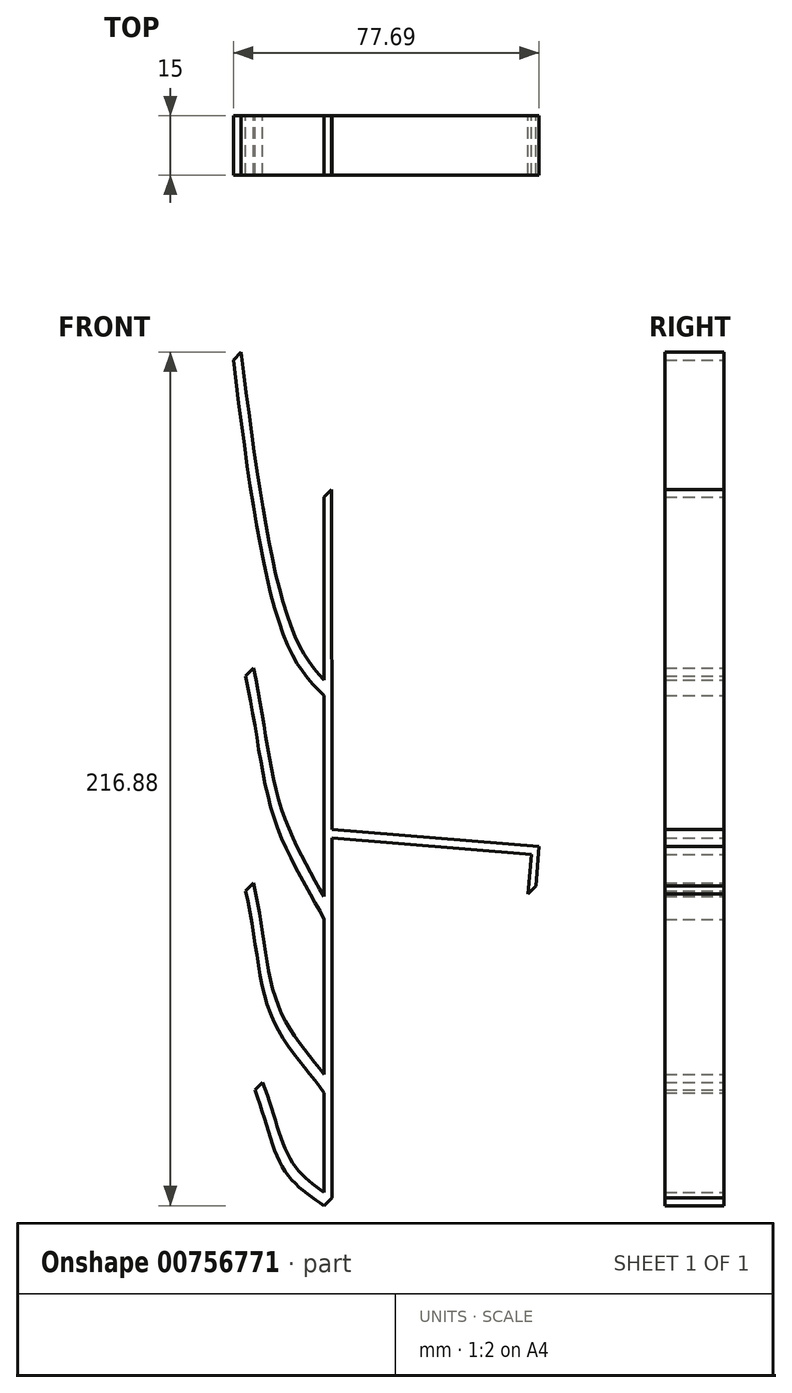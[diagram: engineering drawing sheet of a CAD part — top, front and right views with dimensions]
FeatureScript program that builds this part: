
annotation { "Feature Type Name" : "Feature", "Feature Type Description" : "" }
export const myFeature = defineFeature(function(context is Context, id is Id, definition is map)
    precondition{}
    {
        {
            var Q0;
            Q0=qCreatedBy(makeId("Front.planeOp"),FACE);
            var sketch = newSketch(context, id + "F0", { "sketchPlane" : qUnion([Q0])});
            skLineSegment(sketch, "E0", {"start": v(-0.1, 90) * mm, "end": v(0, -90) * mm});
            skFitSpline(sketch, "E1", {"points": [v(0, -90) * mm, v(-10, -81.14) * mm, v(-17.61, -60.62) * mm], "startDerivative": vector(-24.45, 17.02) * mm, "endDerivative": vector(-15.94, 41.83) * mm});
            skFitSpline(sketch, "E2", {"points": [v(-0.02, -61.3) * mm, v(-13.22, -42.27) * mm, v(-20, -10) * mm], "startDerivative": vector(-24.6, 34.99) * mm, "endDerivative": vector(-15.82, 63.64) * mm});
            skFitSpline(sketch, "E3", {"points": [v(-0.04, -17.24) * mm, v(-12.43, 7.58) * mm, v(-20, 44.6) * mm], "startDerivative": vector(-23.72, 47.01) * mm, "endDerivative": vector(-16.56, 73.06) * mm});
            skFitSpline(sketch, "E4", {"points": [v(-0.08, 39.6) * mm, v(-10, 54.14) * mm, v(-23.09, 124.88) * mm], "startDerivative": vector(-32.68, 30.43) * mm, "endDerivative": vector(-15.5, 126.3) * mm});
            skLineSegment(sketch, "E5", {"start": v(-0.06, 3.61) * mm, "end": v(52.6, -0.78) * mm});
            skLineSegment(sketch, "E6", {"start": v(52.6, -0.78) * mm, "end": v(51.77, -10.75) * mm});
            skPoint(sketch, "E7", {"position": v(7.76, 2.96) * mm});
            skLineSegment(sketch, "E8", {"start": v(-0.1, 90) * mm, "end": v(1.9, 92) * mm, "construction": true});
            skLineSegment(sketch, "E9", {"start": v(1.9, 92) * mm, "end": v(2, -88) * mm});
            skFitSpline(sketch, "E10", {"points": [v(2, -88) * mm, v(-8, -79.14) * mm, v(-15.61, -58.62) * mm], "startDerivative": vector(-24.45, 17.02) * mm, "endDerivative": vector(-15.94, 41.83) * mm});
            skFitSpline(sketch, "E11", {"points": [v(1.98, -59.3) * mm, v(-11.22, -40.27) * mm, v(-18, -8) * mm], "startDerivative": vector(-24.6, 34.99) * mm, "endDerivative": vector(-15.82, 63.64) * mm});
            skFitSpline(sketch, "E12", {"points": [v(1.96, -15.24) * mm, v(-10.43, 9.58) * mm, v(-18, 46.6) * mm], "startDerivative": vector(-23.72, 47.01) * mm, "endDerivative": vector(-16.56, 73.06) * mm});
            skFitSpline(sketch, "E13", {"points": [v(1.92, 41.6) * mm, v(-8, 56.14) * mm, v(-21.09, 126.88) * mm], "startDerivative": vector(-32.68, 30.43) * mm, "endDerivative": vector(-15.5, 126.3) * mm});
            skLineSegment(sketch, "E14", {"start": v(1.94, 5.61) * mm, "end": v(54.6, 1.22) * mm});
            skLineSegment(sketch, "E15", {"start": v(54.6, 1.22) * mm, "end": v(53.77, -8.75) * mm});
            skPoint(sketch, "E16", {"position": v(9.76, 4.96) * mm});
            skLineSegment(sketch, "E17", {"start": v(1.9, 92) * mm, "end": v(3.9, 90) * mm, "construction": true});
            skLineSegment(sketch, "E18", {"start": v(-20, 44.6) * mm, "end": v(-18, 46.6) * mm});
            skLineSegment(sketch, "E19", {"start": v(-23.09, 124.88) * mm, "end": v(-21.09, 126.88) * mm});
            skLineSegment(sketch, "E20", {"start": v(-0.1, 90) * mm, "end": v(1.9, 92) * mm});
            skLineSegment(sketch, "E21", {"start": v(51.77, -10.75) * mm, "end": v(53.77, -8.75) * mm});
            skLineSegment(sketch, "E22", {"start": v(-20, -10) * mm, "end": v(-18, -8) * mm});
            skLineSegment(sketch, "E23", {"start": v(-17.61, -60.62) * mm, "end": v(-15.61, -58.62) * mm});
            skLineSegment(sketch, "E24", {"start": v(0, -90) * mm, "end": v(2, -88) * mm});
            skSolve(sketch);
        }
        {
            var Q0;
            {var subQ0=sQuery(id+"F0.wireOp",EDGE,"E1");Q0=makeQuery(id+"F0.imprint","IMPRINT",FACE,{"disambiguationData":[TD([[makeQuery(id+"F0.imprint","IMPRINT",EDGE,{"derivedFrom":subQ0}),-1.0]])]});}
            var Q1;
            {var subQ0=sQuery(id+"F0.wireOp",EDGE,"E2");Q1=makeQuery(id+"F0.imprint","IMPRINT",FACE,{"disambiguationData":[TD([[makeQuery(id+"F0.imprint","IMPRINT",EDGE,{"derivedFrom":subQ0}),-1.0]])]});}
            var Q2;
            {var subQ0=sQuery(id+"F0.wireOp",EDGE,"E4");Q2=makeQuery(id+"F0.imprint","IMPRINT",FACE,{"disambiguationData":[TD([[makeQuery(id+"F0.imprint","IMPRINT",EDGE,{"derivedFrom":subQ0}),-1.0]])]});}
            var Q3;
            {var subQ3=sQuery(id+"F0.wireOp",EDGE,"E0");var subQ5=makeQuery(id+"F0.imprint","INTERSECT",VERTEX,{"derivedFrom":[subQ3,sQuery(id+"F0.wireOp",EDGE,"E2")]});Q3=makeQuery(id+"F0.imprint","IMPRINT",FACE,{"disambiguationData":[TD([[makeQuery(id+"F0.imprint","IMPRINT",EDGE,{"disambiguationData":[TD([[subQ5,1.0]])],"derivedFrom":subQ3}),1.0]])]});}
            var Q4;
            {var subQ0=sQuery(id+"F0.wireOp",EDGE,"E3");Q4=makeQuery(id+"F0.imprint","IMPRINT",FACE,{"disambiguationData":[TD([[makeQuery(id+"F0.imprint","IMPRINT",EDGE,{"derivedFrom":subQ0}),-1.0]])]});}
            var Q5;
            {var subQ0=sQuery(id+"F0.wireOp",EDGE,"E5");var subQ1=sQuery(id+"F0.wireOp",EDGE,"E0");var subQ2=makeQuery(id+"F0.imprint","INTERSECT",VERTEX,{"derivedFrom":[subQ1,subQ0]});Q5=makeQuery(id+"F0.imprint","IMPRINT",FACE,{"disambiguationData":[TD([[makeQuery(id+"F0.imprint","IMPRINT",EDGE,{"disambiguationData":[TD([[subQ2,-1.0]])],"derivedFrom":subQ1}),1.0]])]});}
            var Q6;
            {var subQ5=sQuery(id+"F0.wireOp",EDGE,"E0");var subQ6=makeQuery(id+"F0.imprint","INTERSECT",VERTEX,{"derivedFrom":[subQ5,sQuery(id+"F0.wireOp",EDGE,"E3")]});Q6=makeQuery(id+"F0.imprint","IMPRINT",FACE,{"disambiguationData":[TD([[makeQuery(id+"F0.imprint","IMPRINT",EDGE,{"disambiguationData":[TD([[subQ6,1.0]])],"derivedFrom":subQ5}),1.0]])]});}
            var Q7;
            {var subQ0=sQuery(id+"F0.wireOp",EDGE,"E20");Q7=makeQuery(id+"F0.imprint","IMPRINT",FACE,{"disambiguationData":[TD([[makeQuery(id+"F0.imprint","IMPRINT",EDGE,{"derivedFrom":subQ0}),-1.0]])]});}
            var Q8;
            {var subQ4=sQuery(id+"F0.wireOp",EDGE,"E6");Q8=makeQuery(id+"F0.imprint","IMPRINT",FACE,{"disambiguationData":[TD([[makeQuery(id+"F0.imprint","IMPRINT",EDGE,{"derivedFrom":subQ4}),1.0]])]});}
            var Q9;
            {var subQ1=sQuery(id+"F0.wireOp",EDGE,"E0");var subQ5=makeQuery(id+"F0.imprint","INTERSECT",VERTEX,{"derivedFrom":[subQ1,sQuery(id+"F0.wireOp",EDGE,"E4")]});Q9=makeQuery(id+"F0.imprint","IMPRINT",FACE,{"disambiguationData":[TD([[makeQuery(id+"F0.imprint","IMPRINT",EDGE,{"disambiguationData":[TD([[subQ5,1.0]])],"derivedFrom":subQ1}),1.0]])]});}
            var Q10;
            {var subQ0=sQuery(id+"F0.wireOp",EDGE,"E24");Q10=makeQuery(id+"F0.imprint","IMPRINT",FACE,{"disambiguationData":[TD([[makeQuery(id+"F0.imprint","IMPRINT",EDGE,{"derivedFrom":subQ0}),1.0]])]});}
            extrude(context, id + "F1", {"entities" : qUnion([Q0, Q1, Q2, Q3, Q4, Q5, Q6, Q7, Q8, Q9, Q10]), "depth" : 15 * mm, "offsetDistance" : 25 * mm});
        }
    });
